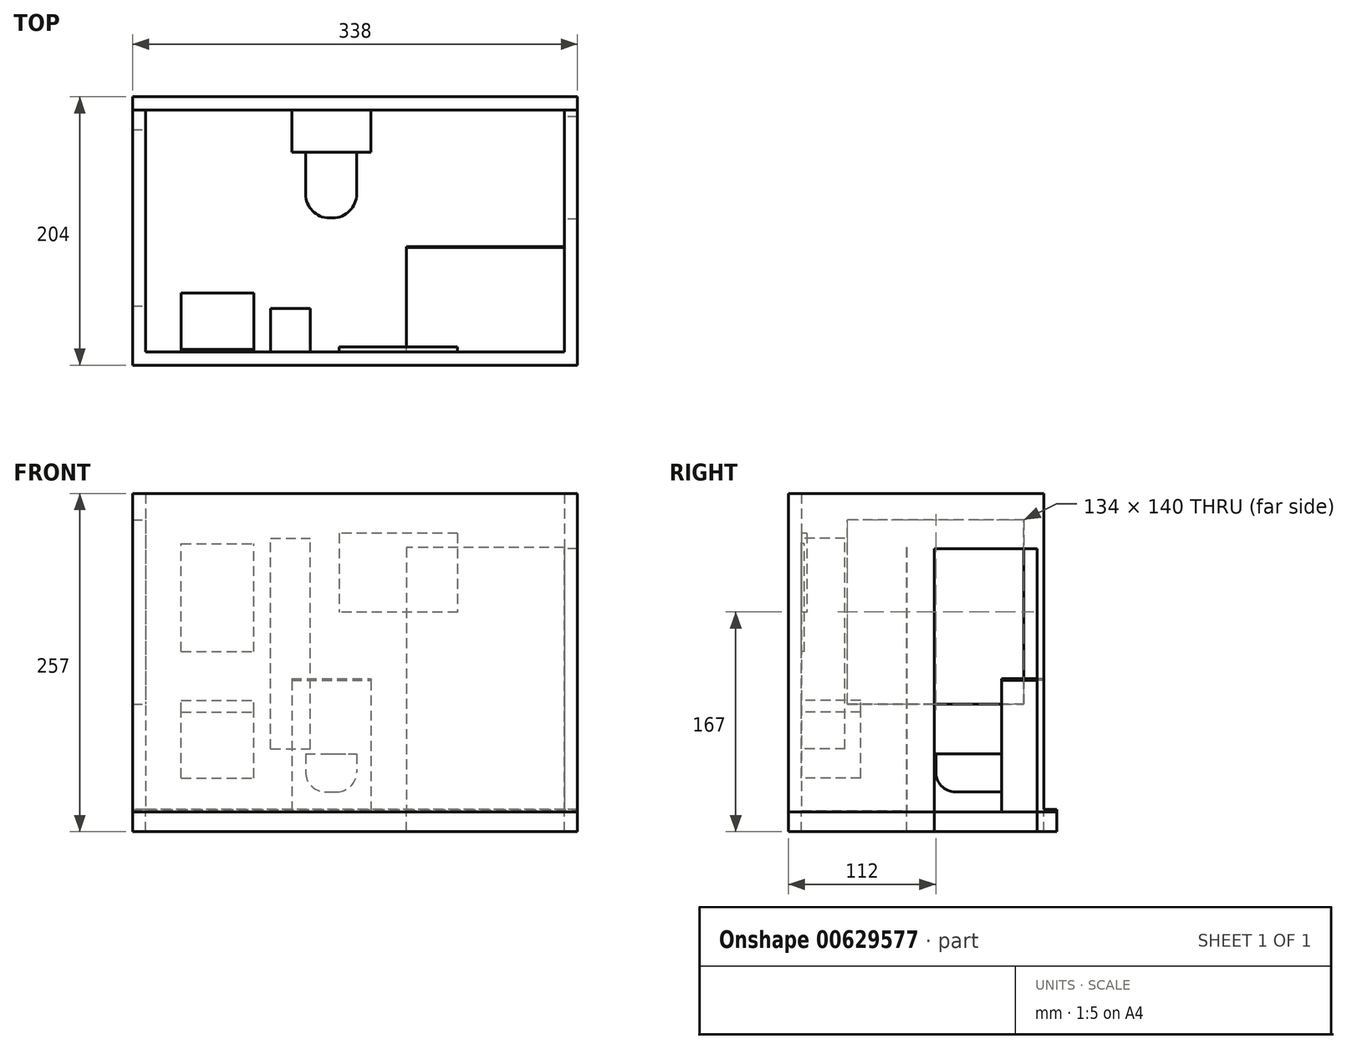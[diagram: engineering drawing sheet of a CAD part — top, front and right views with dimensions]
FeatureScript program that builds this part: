
annotation { "Feature Type Name" : "Feature", "Feature Type Description" : "" }
export const myFeature = defineFeature(function(context is Context, id is Id, definition is map)
    precondition{}
    {
        {
            var Q0;
            Q0=qCreatedBy(makeId("Top.planeOp"),FACE);
            var sketch = newSketch(context, id + "F0", { "sketchPlane" : qUnion([Q0])});
            skLineSegment(sketch, "E0.bottom", {"start": v(0, 0) * mm, "end": v(318, 0) * mm});
            skLineSegment(sketch, "E0.top", {"start": v(0, 184) * mm, "end": v(318, 184) * mm});
            skLineSegment(sketch, "E0.left", {"start": v(0, 0) * mm, "end": v(0, 184) * mm});
            skLineSegment(sketch, "E0.right", {"start": v(318, 0) * mm, "end": v(318, 184) * mm});
            skSolve(sketch);
        }
        {
            var Q0;
            Q0=makeQuery(id+"F0.imprint","IMPRINT",FACE,{"disambiguationData":[TD([[makeQuery(id+"F0.imprint","IMPRINT",EDGE,{"derivedFrom":sQuery(id+"F0.wireOp",EDGE,"E0.bottom")}),1.0]])]});
            extrude(context, id + "F1", {"entities" : qUnion([Q0]), "depth" : 242 * mm, "offsetDistance" : 25 * mm});
        }
        {
            var Q0;
            Q0=makeQuery(id+"F1.opExtrude","CAP_FACE",FACE,{"disambiguationData":[OSD([sQuery(id+"F0.wireOp",EDGE,"E0.bottom"),sQuery(id+"F0.wireOp",EDGE,"E0.top"),sQuery(id+"F0.wireOp",EDGE,"E0.left"),sQuery(id+"F0.wireOp",EDGE,"E0.right")])],"isStart":false});
            shell(context, id + "F2", {"entities" : qUnion([Q0]), "thickness" : 10 * mm, "oppositeDirection" : true});
        }
        {
            var Q0;
            Q0=makeQuery(id+"F2.opShell","OFFSET_FACE",FACE,{"disambiguationData":[OSD([sQuery(id+"F0.wireOp",EDGE,"E0.left")])]});
            var sketch = newSketch(context, id + "F3", { "sketchPlane" : qUnion([Q0])});
            skLineSegment(sketch, "E1.bottom", {"start": v(35, 222) * mm, "end": v(169, 222) * mm});
            skLineSegment(sketch, "E1.top", {"start": v(35, 82) * mm, "end": v(169, 82) * mm});
            skLineSegment(sketch, "E1.left", {"start": v(35, 222) * mm, "end": v(35, 82) * mm});
            skLineSegment(sketch, "E1.right", {"start": v(169, 222) * mm, "end": v(169, 82) * mm});
            skSolve(sketch);
        }
        {
            var Q0;
            Q0=makeQuery(id+"F3.imprint","IMPRINT",FACE,{"disambiguationData":[TD([[makeQuery(id+"F3.imprint","IMPRINT",EDGE,{"derivedFrom":sQuery(id+"F3.wireOp",EDGE,"E1.bottom")}),-1.0]])]});
            extrude(context, id + "F4", {"entities" : qUnion([Q0]), "operationType" : NewBodyOperationType.REMOVE, "oppositeDirection" : true, "depth" : 25 * mm, "offsetDistance" : 25 * mm});
        }
        {
            var Q0;
            Q0=makeQuery(id+"F2.opShell","OFFSET_FACE",FACE,{"disambiguationData":[OSD([sQuery(id+"F0.wireOp",EDGE,"E0.bottom"),sQuery(id+"F0.wireOp",EDGE,"E0.top"),sQuery(id+"F0.wireOp",EDGE,"E0.left"),sQuery(id+"F0.wireOp",EDGE,"E0.right")])]});
            var sketch = newSketch(context, id + "F5", { "sketchPlane" : qUnion([Q0])});
            skLineSegment(sketch, "E2.bottom", {"start": v(318, 0) * mm, "end": v(198, 0) * mm});
            skLineSegment(sketch, "E2.top", {"start": v(318, 80) * mm, "end": v(198, 80) * mm});
            skLineSegment(sketch, "E2.left", {"start": v(318, 0) * mm, "end": v(318, 80) * mm});
            skLineSegment(sketch, "E2.right", {"start": v(198, 0) * mm, "end": v(198, 80) * mm});
            skSolve(sketch);
        }
        {
            var Q0;
            Q0=makeQuery(id+"F5.imprint","IMPRINT",FACE,{"disambiguationData":[TD([[makeQuery(id+"F5.imprint","IMPRINT",EDGE,{"derivedFrom":sQuery(id+"F5.wireOp",EDGE,"E2.bottom")}),1.0]])]});
            extrude(context, id + "F6", {"entities" : qUnion([Q0]), "operationType" : NewBodyOperationType.ADD, "depth" : 1 * mm, "offsetDistance" : 25 * mm});
        }
        {
            var Q0;
            Q0=makeQuery(id+"F6.opExtrude","CAP_FACE",FACE,{"disambiguationData":[OSD([sQuery(id+"F5.wireOp",EDGE,"E2.bottom"),sQuery(id+"F5.wireOp",EDGE,"E2.top"),sQuery(id+"F5.wireOp",EDGE,"E2.left"),sQuery(id+"F5.wireOp",EDGE,"E2.right")])],"isStart":false});
            var sketch = newSketch(context, id + "F7", { "sketchPlane" : qUnion([Q0])});
            skLineSegment(sketch, "E3.bottom", {"start": v(318, 80) * mm, "end": v(198, 80) * mm});
            skLineSegment(sketch, "E3.top", {"start": v(318, 79.5) * mm, "end": v(198, 79.5) * mm});
            skLineSegment(sketch, "E3.left", {"start": v(318, 80) * mm, "end": v(318, 79.5) * mm});
            skLineSegment(sketch, "E3.right", {"start": v(198, 80) * mm, "end": v(198, 79.5) * mm});
            skSolve(sketch);
        }
        {
            var Q0;
            Q0=makeQuery(id+"F7.imprint","IMPRINT",FACE,{"disambiguationData":[TD([[makeQuery(id+"F7.imprint","IMPRINT",EDGE,{"derivedFrom":sQuery(id+"F7.wireOp",EDGE,"E3.bottom")}),1.0]])]});
            extrude(context, id + "F8", {"entities" : qUnion([Q0]), "depth" : 200 * mm, "offsetDistance" : 25 * mm});
        }
        {
            var Q0;
            Q0=makeQuery(id+"F2.opShell","OFFSET_FACE",FACE,{"disambiguationData":[OSD([sQuery(id+"F0.wireOp",EDGE,"E0.right")])]});
            var sketch = newSketch(context, id + "F9", { "sketchPlane" : qUnion([Q0])});
            skLineSegment(sketch, "E4.bottom", {"start": v(-179, 0) * mm, "end": v(-101, 0) * mm});
            skLineSegment(sketch, "E4.top", {"start": v(-179, 200) * mm, "end": v(-101, 200) * mm});
            skLineSegment(sketch, "E4.left", {"start": v(-179, 0) * mm, "end": v(-179, 200) * mm});
            skLineSegment(sketch, "E4.right", {"start": v(-101, 0) * mm, "end": v(-101, 200) * mm});
            skSolve(sketch);
        }
        {
            var Q0;
            Q0=makeQuery(id+"F9.imprint","IMPRINT",FACE,{"disambiguationData":[TD([[makeQuery(id+"F9.imprint","IMPRINT",EDGE,{"derivedFrom":sQuery(id+"F9.wireOp",EDGE,"E4.bottom")}),-1.0]])]});
            extrude(context, id + "F10", {"entities" : qUnion([Q0]), "operationType" : NewBodyOperationType.REMOVE, "oppositeDirection" : true, "depth" : 25 * mm, "offsetDistance" : 25 * mm});
        }
        {
            var Q0;
            Q0=makeQuery(id+"F10.boolean.opBoolean","MERGE",FACE,{"derivedFrom":[makeQuery(id+"F2.opShell","OFFSET_FACE",FACE,{"disambiguationData":[OSD([sQuery(id+"F0.wireOp",EDGE,"E0.bottom"),sQuery(id+"F0.wireOp",EDGE,"E0.top"),sQuery(id+"F0.wireOp",EDGE,"E0.left"),sQuery(id+"F0.wireOp",EDGE,"E0.right")])]}),makeQuery(id+"F10.opExtrude","SWEPT_FACE",FACE,{"disambiguationData":[OSD([sQuery(id+"F9.wireOp",EDGE,"E4.bottom")])]})]});
            var sketch = newSketch(context, id + "F11", { "sketchPlane" : qUnion([Q0])});
            skLineSegment(sketch, "E5.bottom", {"start": v(171, 184) * mm, "end": v(111, 184) * mm});
            skLineSegment(sketch, "E5.top", {"start": v(171, 152) * mm, "end": v(111, 152) * mm});
            skLineSegment(sketch, "E5.left", {"start": v(171, 184) * mm, "end": v(171, 152) * mm});
            skLineSegment(sketch, "E5.right", {"start": v(111, 184) * mm, "end": v(111, 152) * mm});
            skSolve(sketch);
        }
        {
            var Q0;
            Q0=makeQuery(id+"F11.imprint","IMPRINT",FACE,{"disambiguationData":[TD([[makeQuery(id+"F11.imprint","IMPRINT",EDGE,{"derivedFrom":sQuery(id+"F11.wireOp",EDGE,"E5.bottom")}),-1.0]])]});
            extrude(context, id + "F12", {"entities" : qUnion([Q0]), "depth" : 100 * mm, "offsetDistance" : 25 * mm});
        }
        {
            var Q0;
            Q0=makeQuery(id+"F2.opShell","OFFSET_FACE",FACE,{"disambiguationData":[OSD([sQuery(id+"F0.wireOp",EDGE,"E0.bottom")])]});
            var sketch = newSketch(context, id + "F13", { "sketchPlane" : qUnion([Q0])});
            skLineSegment(sketch, "E6.bottom", {"start": v(-27.08, 75.81) * mm, "end": v(-82.08, 75.81) * mm});
            skLineSegment(sketch, "E6.top", {"start": v(-27.08, 84.81) * mm, "end": v(-82.08, 84.81) * mm});
            skLineSegment(sketch, "E6.left", {"start": v(-27.08, 75.81) * mm, "end": v(-27.08, 84.81) * mm});
            skLineSegment(sketch, "E6.right", {"start": v(-82.08, 75.81) * mm, "end": v(-82.08, 84.81) * mm});
            skSolve(sketch);
        }
        {
            var Q0;
            Q0 = qSketchRegion(id + "F13", true);
            extrude(context, id + "F14", {"entities" : qUnion([Q0]), "depth" : 45 * mm, "offsetDistance" : 25 * mm});
        }
        {
            var Q0;
            Q0=makeQuery(id+"F14.opExtrude","SWEPT_FACE",FACE,{"disambiguationData":[OSD([sQuery(id+"F13.wireOp",EDGE,"E6.bottom")])]});
            var sketch = newSketch(context, id + "F15", { "sketchPlane" : qUnion([Q0])});
            skSolve(sketch);
        }
        {
            var Q0;
            Q0 = qSketchRegion(id + "F15", true);
            var Q1;
            {var subQ0=sQuery(id+"F13.wireOp",EDGE,"E6.bottom");Q1=makeQuery(id+"F15.imprint","IMPRINT",FACE,{"disambiguationData":[TD([[makeQuery(id+"F15.imprint","IMPRINT",EDGE,{"derivedFrom":makeQuery(id+"F14.opExtrude","CAP_EDGE",EDGE,{"disambiguationData":[OSD([subQ0])],"isStart":true})}),-1.0]])]});}
            extrude(context, id + "F16", {"entities" : qUnion([Q0, Q1]), "depth" : 50 * mm, "offsetDistance" : 25 * mm});
        }
        {
            var Q0;
            Q0=makeQuery(id+"F12.opExtrude","CAP_FACE",FACE,{"disambiguationData":[OSD([sQuery(id+"F11.wireOp",EDGE,"E5.bottom"),sQuery(id+"F11.wireOp",EDGE,"E5.top"),sQuery(id+"F11.wireOp",EDGE,"E5.left"),sQuery(id+"F11.wireOp",EDGE,"E5.right")])],"isStart":false});
            extrude(context, id + "F17", {"entities" : qUnion([Q0]), "depth" : 1.2 * mm, "offsetDistance" : 25 * mm});
        }
        {
            var Q0;
            Q0=makeQuery(id+"F2.opShell","OFFSET_FACE",FACE,{"disambiguationData":[OSD([sQuery(id+"F0.wireOp",EDGE,"E0.bottom")])]});
            var sketch = newSketch(context, id + "F18", { "sketchPlane" : qUnion([Q0])});
            skLineSegment(sketch, "E7.bottom", {"start": v(-27.08, 121.81) * mm, "end": v(-82.08, 121.81) * mm});
            skLineSegment(sketch, "E7.top", {"start": v(-27.08, 203.81) * mm, "end": v(-82.08, 203.81) * mm});
            skLineSegment(sketch, "E7.left", {"start": v(-27.08, 121.81) * mm, "end": v(-27.08, 203.81) * mm});
            skLineSegment(sketch, "E7.right", {"start": v(-82.08, 121.81) * mm, "end": v(-82.08, 203.81) * mm});
            skSolve(sketch);
        }
        {
            var Q0;
            Q0=makeQuery(id+"F18.imprint","IMPRINT",FACE,{"disambiguationData":[TD([[makeQuery(id+"F18.imprint","IMPRINT",EDGE,{"derivedFrom":sQuery(id+"F18.wireOp",EDGE,"E7.bottom")}),-1.0]])]});
            extrude(context, id + "F19", {"entities" : qUnion([Q0]), "depth" : 2 * mm, "offsetDistance" : 25 * mm});
        }
        {
            var Q0;
            Q0=makeQuery(id+"F12.opExtrude","SWEPT_FACE",FACE,{"disambiguationData":[OSD([sQuery(id+"F11.wireOp",EDGE,"E5.top")])]});
            var sketch = newSketch(context, id + "F20", { "sketchPlane" : qUnion([Q0])});
            skLineSegment(sketch, "E8.bottom", {"start": v(121.47, 44.02) * mm, "end": v(160.3, 44.02) * mm});
            skLineSegment(sketch, "E8.top", {"start": v(121.47, 15.3) * mm, "end": v(160.3, 15.3) * mm});
            skLineSegment(sketch, "E8.left", {"start": v(121.47, 44.02) * mm, "end": v(121.47, 15.3) * mm});
            skLineSegment(sketch, "E8.right", {"start": v(160.3, 44.02) * mm, "end": v(160.3, 15.3) * mm});
            skSolve(sketch);
        }
        {
            var Q0;
            Q0=makeQuery(id+"F20.imprint","IMPRINT",FACE,{"disambiguationData":[TD([[makeQuery(id+"F20.imprint","IMPRINT",EDGE,{"derivedFrom":sQuery(id+"F20.wireOp",EDGE,"E8.bottom")}),-1.0]])]});
            extrude(context, id + "F21", {"entities" : qUnion([Q0]), "depth" : 50 * mm, "offsetDistance" : 25 * mm});
        }
        {
            var Q0;
            Q0=makeQuery(id+"F21.opExtrude","CAP_EDGE",EDGE,{"disambiguationData":[OSD([sQuery(id+"F20.wireOp",EDGE,"E8.right")])],"isStart":false});
            var Q1;
            Q1=makeQuery(id+"F21.opExtrude","CAP_EDGE",EDGE,{"disambiguationData":[OSD([sQuery(id+"F20.wireOp",EDGE,"E8.left")])],"isStart":false});
            fillet(context, id + "F22", {"entities" : qUnion([Q0, Q1]), "radius" : 18 * mm, "tangentPropagation" : true, "allowEdgeOverflow" : false});
        }
        {
            var Q0;
            Q0=makeQuery(id+"F21.opExtrude","SWEPT_EDGE",EDGE,{"disambiguationData":[OSD([sQuery(id+"F20.wireOp",EDGE,"E8.top"),sQuery(id+"F20.wireOp",EDGE,"E8.right")])]});
            var Q1;
            Q1=makeQuery(id+"F22.opFillet","BLEND_EDGE",EDGE,{"blendedFrom":[makeQuery(id+"F21.opExtrude","CAP_EDGE",EDGE,{"disambiguationData":[OSD([sQuery(id+"F20.wireOp",EDGE,"E8.right")])],"isStart":false}),makeQuery(id+"F21.opExtrude","SWEPT_FACE",FACE,{"disambiguationData":[OSD([sQuery(id+"F20.wireOp",EDGE,"E8.top")])]})],"blendedInto":[makeQuery(id+"F21.opExtrude","SWEPT_FACE",FACE,{"disambiguationData":[OSD([sQuery(id+"F20.wireOp",EDGE,"E8.top")])]})]});
            fillet(context, id + "F23", {"entities" : qUnion([Q0, Q1]), "radius" : 15 * mm, "tangentPropagation" : true, "allowEdgeOverflow" : false});
        }
        {
            var Q0;
            Q0=makeQuery(id+"F1.opExtrude","CAP_FACE",FACE,{"disambiguationData":[OSD([sQuery(id+"F0.wireOp",EDGE,"E0.bottom"),sQuery(id+"F0.wireOp",EDGE,"E0.top"),sQuery(id+"F0.wireOp",EDGE,"E0.left"),sQuery(id+"F0.wireOp",EDGE,"E0.right")])],"isStart":true});
            var sketch = newSketch(context, id + "F24", { "sketchPlane" : qUnion([Q0])});
            skSolve(sketch);
        }
        {
            var Q0;
            Q0 = qSketchRegion(id + "F24", true);
            var Q1;
            Q1=makeQuery(id+"F24.imprint","IMPRINT",FACE,{"disambiguationData":[TD([[makeQuery(id+"F24.imprint","IMPRINT",EDGE,{"derivedFrom":makeQuery(id+"F1.opExtrude","CAP_EDGE",EDGE,{"disambiguationData":[OSD([sQuery(id+"F0.wireOp",EDGE,"E0.bottom")])],"isStart":true})}),-1.0]])]});
            extrude(context, id + "F25", {"entities" : qUnion([Q0, Q1]), "operationType" : NewBodyOperationType.REMOVE, "oppositeDirection" : true, "depth" : 10 * mm, "offsetDistance" : 25 * mm});
        }
        {
            var Q0;
            Q0=makeQuery(id+"F25.boolean.opBoolean","COPY",FACE,{"derivedFrom":makeQuery(id+"F25.opExtrude","CAP_FACE",FACE,{"disambiguationData":[OSD([sQuery(id+"F0.wireOp",EDGE,"E0.bottom"),sQuery(id+"F0.wireOp",EDGE,"E0.top"),sQuery(id+"F0.wireOp",EDGE,"E0.left"),sQuery(id+"F0.wireOp",EDGE,"E0.right")])],"isStart":false})});
            var sketch = newSketch(context, id + "F26", { "sketchPlane" : qUnion([Q0])});
            skLineSegment(sketch, "E9.bottom", {"start": v(328, 10) * mm, "end": v(-10, 10) * mm});
            skLineSegment(sketch, "E9.top", {"start": v(328, -194) * mm, "end": v(-10, -194) * mm});
            skLineSegment(sketch, "E9.left", {"start": v(328, 10) * mm, "end": v(328, -194) * mm});
            skLineSegment(sketch, "E9.right", {"start": v(-10, 10) * mm, "end": v(-10, -194) * mm});
            skSolve(sketch);
        }
        {
            var Q0;
            {var subQ10=sQuery(id+"F5.wireOp",EDGE,"E2.top");Q0=makeQuery(id+"F26.imprint","IMPRINT",FACE,{"disambiguationData":[TD([[makeQuery(id+"F26.imprint","IMPRINT",EDGE,{"derivedFrom":makeQuery(id+"F6.opExtrude","CAP_EDGE",EDGE,{"disambiguationData":[OSD([subQ10])],"isStart":true})}),1.0]])]});}
            var Q1;
            {var subQ4=sQuery(id+"F26.wireOp",EDGE,"E9.bottom");Q1=makeQuery(id+"F26.imprint","IMPRINT",FACE,{"disambiguationData":[TD([[makeQuery(id+"F26.imprint","IMPRINT",EDGE,{"derivedFrom":subQ4}),-1.0]])]});}
            extrude(context, id + "F27", {"entities" : qUnion([Q0, Q1]), "depth" : 15 * mm, "offsetDistance" : 25 * mm});
        }
        {
            var Q0;
            Q0=makeQuery(id+"F2.opShell","OFFSET_FACE",FACE,{"disambiguationData":[OSD([sQuery(id+"F0.wireOp",EDGE,"E0.bottom")])]});
            var sketch = newSketch(context, id + "F28", { "sketchPlane" : qUnion([Q0])});
            skLineSegment(sketch, "E10.bottom", {"start": v(-95.04, 47.95) * mm, "end": v(-125.04, 47.95) * mm});
            skLineSegment(sketch, "E10.top", {"start": v(-95.04, 207.95) * mm, "end": v(-125.04, 207.95) * mm});
            skLineSegment(sketch, "E10.left", {"start": v(-95.04, 47.95) * mm, "end": v(-95.04, 207.95) * mm});
            skLineSegment(sketch, "E10.right", {"start": v(-125.04, 47.95) * mm, "end": v(-125.04, 207.95) * mm});
            skSolve(sketch);
        }
        {
            var Q0;
            Q0=makeQuery(id+"F28.imprint","IMPRINT",FACE,{"disambiguationData":[TD([[makeQuery(id+"F28.imprint","IMPRINT",EDGE,{"derivedFrom":sQuery(id+"F28.wireOp",EDGE,"E10.bottom")}),-1.0]])]});
            extrude(context, id + "F29", {"entities" : qUnion([Q0]), "depth" : 33 * mm, "offsetDistance" : 25 * mm});
        }
        {
            var Q0;
            Q0=makeQuery(id+"F2.opShell","OFFSET_FACE",FACE,{"disambiguationData":[OSD([sQuery(id+"F0.wireOp",EDGE,"E0.bottom")])]});
            var sketch = newSketch(context, id + "F30", { "sketchPlane" : qUnion([Q0])});
            skLineSegment(sketch, "E11.bottom", {"start": v(-236.88, 211.66) * mm, "end": v(-146.88, 211.66) * mm});
            skLineSegment(sketch, "E11.top", {"start": v(-236.88, 151.66) * mm, "end": v(-146.88, 151.66) * mm});
            skLineSegment(sketch, "E11.left", {"start": v(-236.88, 211.66) * mm, "end": v(-236.88, 151.66) * mm});
            skLineSegment(sketch, "E11.right", {"start": v(-146.88, 211.66) * mm, "end": v(-146.88, 151.66) * mm});
            skSolve(sketch);
        }
        {
            var Q0;
            Q0=makeQuery(id+"F30.imprint","IMPRINT",FACE,{"disambiguationData":[TD([[makeQuery(id+"F30.imprint","IMPRINT",EDGE,{"derivedFrom":sQuery(id+"F30.wireOp",EDGE,"E11.bottom")}),-1.0]])]});
            extrude(context, id + "F31", {"entities" : qUnion([Q0]), "depth" : 4 * mm, "offsetDistance" : 25 * mm});
        }
        {
            var Q0;
            Q0=makeQuery(id+"F1.opExtrude","CAP_FACE",FACE,{"disambiguationData":[OSD([sQuery(id+"F0.wireOp",EDGE,"E0.bottom"),sQuery(id+"F0.wireOp",EDGE,"E0.top"),sQuery(id+"F0.wireOp",EDGE,"E0.left"),sQuery(id+"F0.wireOp",EDGE,"E0.right")])],"isStart":false});
            var sketch = newSketch(context, id + "F32", { "sketchPlane" : qUnion([Q0])});
            skLineSegment(sketch, "E12.bottom", {"start": v(328, 194) * mm, "end": v(-10, 194) * mm});
            skLineSegment(sketch, "E12.top", {"start": v(328, 184) * mm, "end": v(-10, 184) * mm});
            skLineSegment(sketch, "E12.left", {"start": v(328, 194) * mm, "end": v(328, 184) * mm});
            skLineSegment(sketch, "E12.right", {"start": v(-10, 194) * mm, "end": v(-10, 184) * mm});
            skSolve(sketch);
        }
        {
            var Q0;
            Q0=makeQuery(id+"F32.imprint","IMPRINT",FACE,{"disambiguationData":[TD([[makeQuery(id+"F32.imprint","IMPRINT",EDGE,{"derivedFrom":sQuery(id+"F32.wireOp",EDGE,"E12.bottom")}),-1.0]])]});
            extrude(context, id + "F33", {"entities" : qUnion([Q0]), "operationType" : NewBodyOperationType.REMOVE, "oppositeDirection" : true, "depth" : 240 * mm, "offsetDistance" : 25 * mm});
        }
    });
